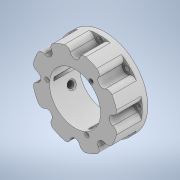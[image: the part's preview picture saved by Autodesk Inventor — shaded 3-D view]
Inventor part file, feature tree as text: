
AUTODESK INVENTOR PART (.ipt)
format: ipt  version: 2021 (Build 250183000, 183)  size: 259,072 bytes
history: native  units: mm
features: sketch x6, extrude x5, pattern_circular x2, hole x1, fillet x1, plane x1, chamfer x1
ambient origin geometry x8: Origin, YZ Plane, XZ Plane, XY Plane, X Axis, Y Axis, Z Axis, Center Point
bodies: Solid1 (feature_tree)
feature tree (17):
  extrude  "Extrusion1"  Depth=41.75mm
  hole  "Hole1"  [1 undecoded]
  fillet  "Fillet1"  Radius=4.0mm
  pattern_circular  "Circular Pattern1"  Count=8 Angle=360.0deg
  plane  "Work Plane1"
  extrude  "Extrusion2"  Depth=8.0mm
  extrude  "Extrusion3"  TaperAngle=0.0deg  [1 undecoded]
  extrude  "Extrusion4"  Depth=0.2mm
  pattern_circular  "Circular Pattern2"  [2 undecoded]
  chamfer  "Chamfer1"  Distance=5.3mm
  extrude  "Extrusion5"  Depth=0.2mm TaperAngle=0.0deg
  sketch  "Sketch1"  dims[d0=70.0mm d1=41.75mm]
  sketch  "Sketch2"  dims[d2=24.45mm d3=0.0mm d4=64.0mm]
  sketch  "Sketch3"  dims[d5=4.5mm d6=6.0mm d7=8.0mm d8=20.0mm d9=90.0deg d10=8.0mm d11=0.0mm d12=4.0mm d13=80.0mm d14=360.0deg]
  sketch  "Sketch4"  dims[d16=22.5deg d17=8.0mm]
  sketch  "Sketch5"  dims[d18=5.0mm d19=0.0mm d20=0.0mm]
  sketch  "Sketch6"  dims[d21=46.0mm d22=3.5mm d23=40.75mm d24=0.0mm d25=5.3mm d26=21.0mm d27=0.0mm d28=30.0mm d29=360.0deg d31=6.108652mm d32=1.0mm d33=2.0mm d34=45.0deg d35=0.2mm d36=0.0mm]
note: 4 required parameter values undecoded (feature->parameter linkage not recoverable at this tier; creation-order binding heuristic only, values carry confidence <= 0.55)
